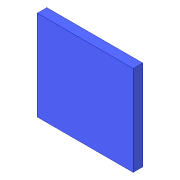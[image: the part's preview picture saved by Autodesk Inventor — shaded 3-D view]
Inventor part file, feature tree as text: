
AUTODESK INVENTOR PART (.ipt)
format: ipt  version: 2018.3 (Build 223284000, 284)  size: 79,360 bytes
history: native  units: in
note: dims shown in document units (in); Inventor stores cm internally (conversion verified against a paired STEP export)
features: extrude x1, sketch x1
ambient origin geometry x8: Origin, YZ Plane, XZ Plane, XY Plane, X Axis, Y Axis, Z Axis, Center Point
bodies: Solid1 (feature_tree)
feature tree (2):
  extrude  "Extrusion1"  Depth=0.75in
  sketch  "Sketch1"  dims[d0=0.8in d1=0.75in d2=0.08in d3=0.0in]
